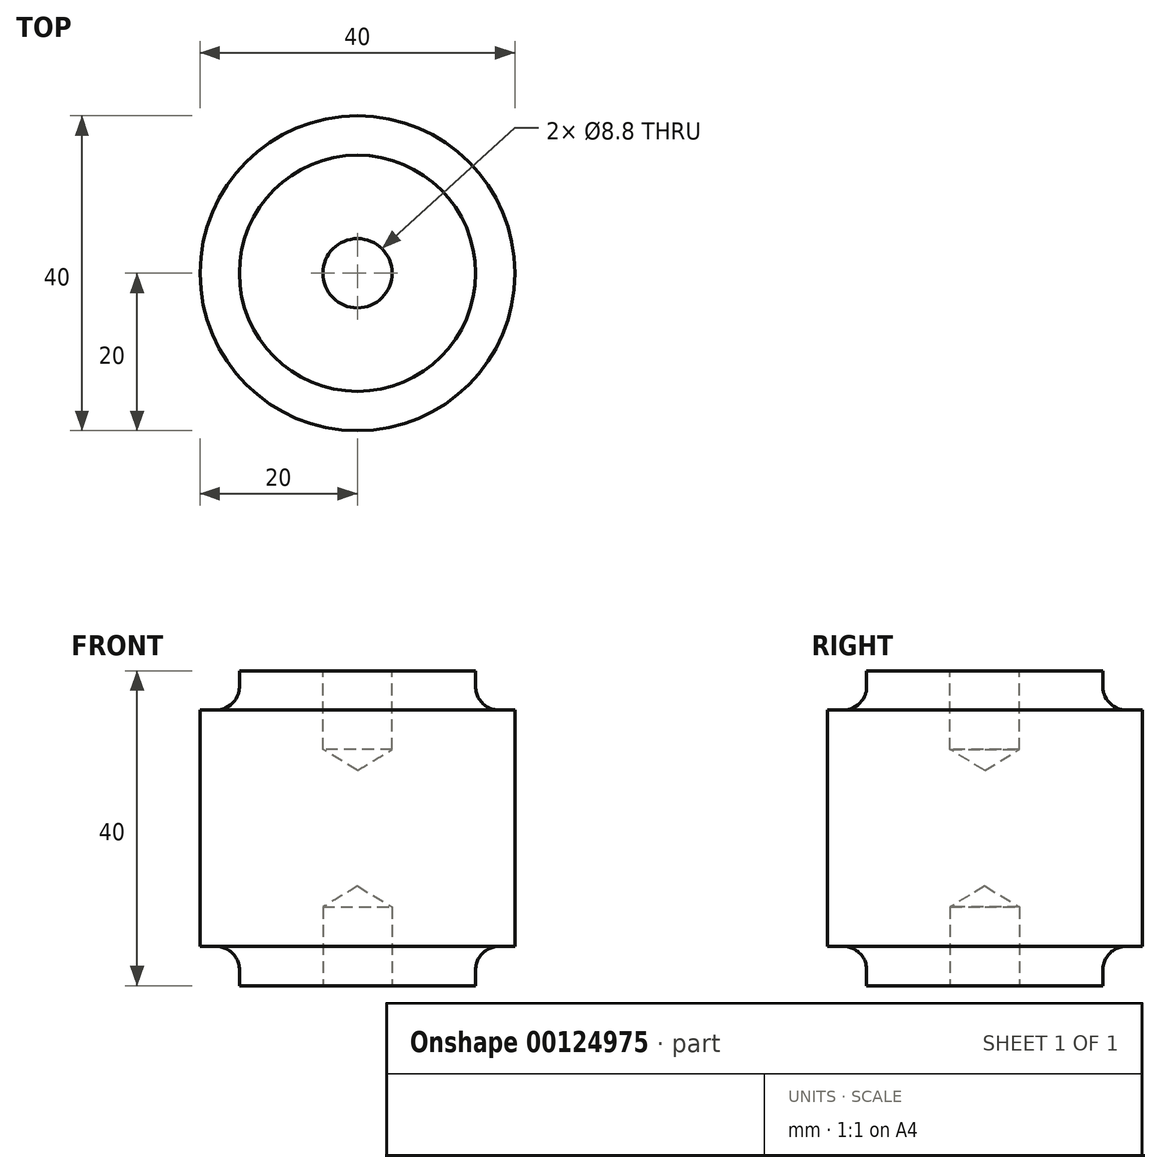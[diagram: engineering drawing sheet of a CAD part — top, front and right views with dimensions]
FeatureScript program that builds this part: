
annotation { "Feature Type Name" : "Feature", "Feature Type Description" : "" }
export const myFeature = defineFeature(function(context is Context, id is Id, definition is map)
    precondition{}
    {
        {
            var Q0;
            Q0=qCreatedBy(makeId("Front.planeOp"),FACE);
            var sketch = newSketch(context, id + "F0", { "sketchPlane" : qUnion([Q0])});
            skPoint(sketch, "E0.middle", {"position": v(0, 0) * mm});
            skLineSegment(sketch, "E1.0", {"start": v(0, 20) * mm, "end": v(-15, 20) * mm});
            skLineSegment(sketch, "E1.2", {"start": v(0, -20) * mm, "end": v(-15, -20) * mm});
            skLineSegment(sketch, "E1.3", {"start": v(-20, 15) * mm, "end": v(-20, -15) * mm});
            skLineSegment(sketch, "E2.bottom", {"start": v(-15, 15) * mm, "end": v(-20, 15) * mm});
            skLineSegment(sketch, "E2.left", {"start": v(-15, 15) * mm, "end": v(-15, 20) * mm});
            skLineSegment(sketch, "E3.bottom", {"start": v(-15, -15) * mm, "end": v(-20, -15) * mm});
            skLineSegment(sketch, "E3.left", {"start": v(-15, -15) * mm, "end": v(-15, -20) * mm});
            skLineSegment(sketch, "E4.left", {"start": v(0, 20) * mm, "end": v(0, -20) * mm});
            skSolve(sketch);
        }
        {
            var Q0;
            Q0=makeQuery(id+"F0.imprint","IMPRINT",FACE,{"disambiguationData":[TD([[makeQuery(id+"F0.imprint","IMPRINT",EDGE,{"derivedFrom":sQuery(id+"F0.wireOp",EDGE,"E1.0")}),1.0]])]});
            var Q1;
            Q1=sQuery(id+"F0.wireOp",EDGE,"E4.left");
            revolve(context, id + "F1", {"entities" : qUnion([Q0]), "axis" : qUnion([Q1]), "revolveType" : RevolveType.FULL});
        }
        {
            var Q0;
            Q0=makeQuery(id+"F1.opRevolve","SWEPT_EDGE",EDGE,{"disambiguationData":[OSD([sQuery(id+"F0.wireOp",EDGE,"E2.bottom"),sQuery(id+"F0.wireOp",EDGE,"E2.left")])]});
            var Q1;
            Q1=makeQuery(id+"F1.opRevolve","SWEPT_EDGE",EDGE,{"disambiguationData":[OSD([sQuery(id+"F0.wireOp",EDGE,"E3.bottom"),sQuery(id+"F0.wireOp",EDGE,"E3.left")])]});
            fillet(context, id + "F2", {"entities" : qUnion([Q0, Q1]), "radius" : 3 * mm, "tangentPropagation" : true, "allowEdgeOverflow" : false});
        }
        {
            var Q0;
            Q0=makeQuery(id+"F1.opRevolve","SWEPT_FACE",FACE,{"disambiguationData":[OSD([sQuery(id+"F0.wireOp",EDGE,"E1.0")])]});
            var sketch = newSketch(context, id + "F3", { "sketchPlane" : qUnion([Q0])});
            skPoint(sketch, "E5", {"position": v(0, 0) * mm});
            skSolve(sketch);
        }
        {
            var Q0;
            Q0=makeQuery(id+"F1.opRevolve","SWEPT_FACE",FACE,{"disambiguationData":[OSD([sQuery(id+"F0.wireOp",EDGE,"E1.2")])]});
            var sketch = newSketch(context, id + "F4", { "sketchPlane" : qUnion([Q0])});
            skPoint(sketch, "E6", {"position": v(0, 0) * mm});
            skSolve(sketch);
        }
        {
            var Q0;
            Q0=sQuery(id+"F4.wireOp",VERTEX,"E6");
            var Q1;
            Q1=sQuery(id+"F3.wireOp",VERTEX,"E5");
            var Q2;
            Q2=makeQuery(id+"F1.opRevolve","SWEPT_BODY",BODY,{"disambiguationData":[OSD([sQuery(id+"F0.wireOp",EDGE,"E1.0"),sQuery(id+"F0.wireOp",EDGE,"E1.2"),sQuery(id+"F0.wireOp",EDGE,"E1.3"),sQuery(id+"F0.wireOp",EDGE,"E2.bottom"),sQuery(id+"F0.wireOp",EDGE,"E2.left"),sQuery(id+"F0.wireOp",EDGE,"E3.bottom"),sQuery(id+"F0.wireOp",EDGE,"E3.left"),sQuery(id+"F0.wireOp",EDGE,"E4.left")])]});
            hole(context, id + "F5", {"style" : HoleStyle.SIMPLE, "endStyle" : HoleEndStyle.BLIND, "standardTappedOrClearance" : lookupTablePath({ "standard" : "ISO", "fit" : "Normal", "size" : "M8", "type" : "Clearance" }), "standardBlindInLast" : lookupTablePath({ "fit" : "Standard", "standard" : "ISO", "size" : "M8", "type" : "Clearance" }), "holeDiameter" : 8.8 * mm, "holeDepth" : 10 * mm, "locations" : qUnion([Q0, Q1]), "scope" : qUnion([Q2])});
        }
    });
